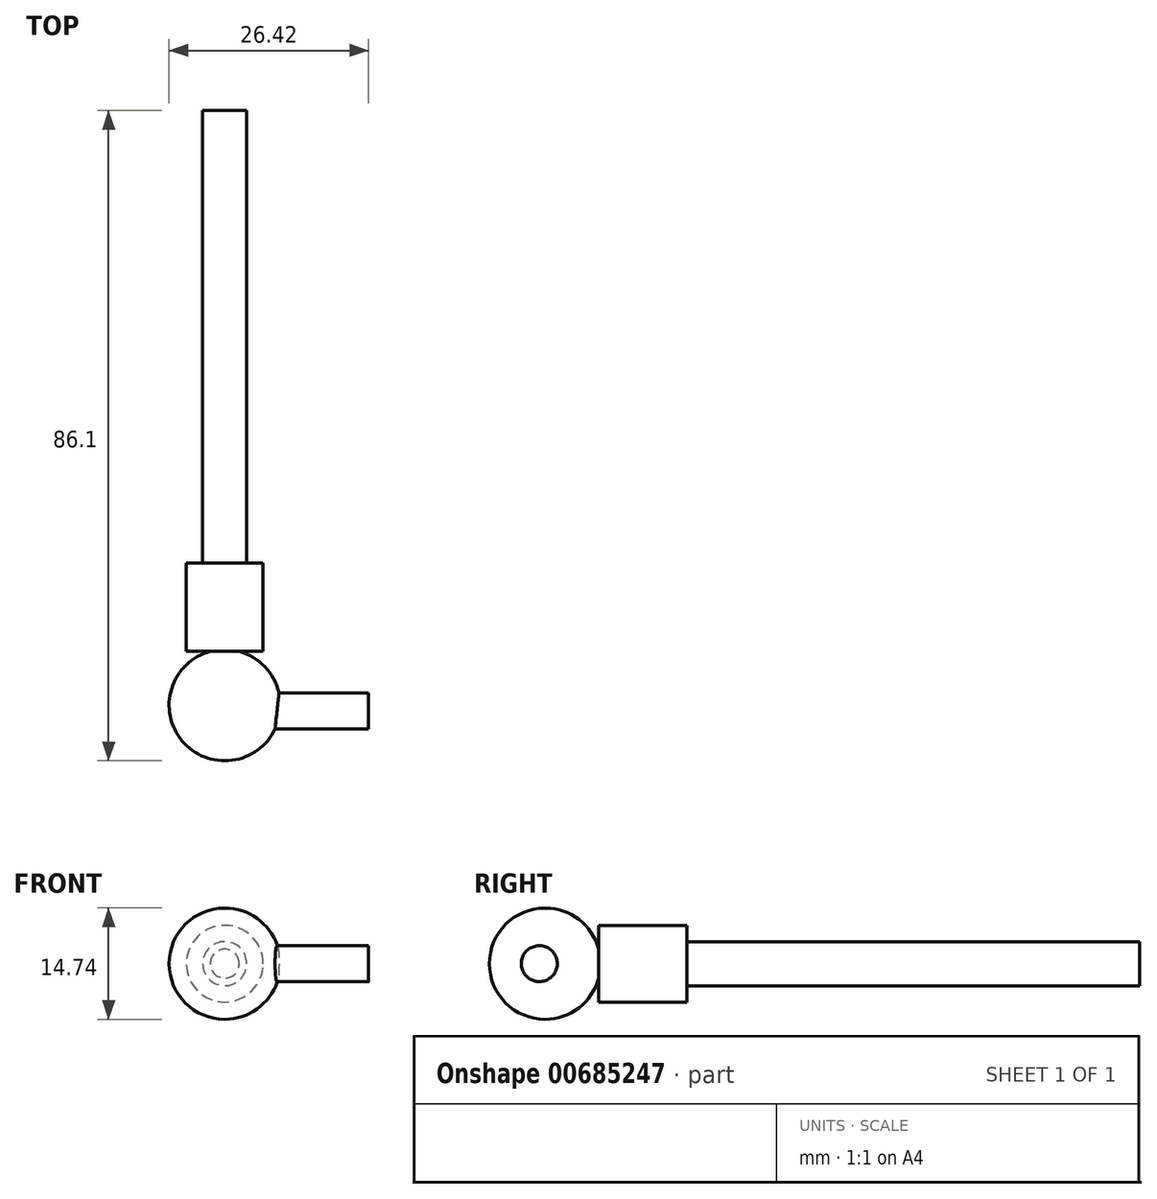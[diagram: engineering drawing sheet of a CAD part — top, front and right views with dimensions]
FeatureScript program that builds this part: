
annotation { "Feature Type Name" : "Feature", "Feature Type Description" : "" }
export const myFeature = defineFeature(function(context is Context, id is Id, definition is map)
    precondition{}
    {
        {
            var Q0;
            Q0=qCreatedBy(makeId("Front.planeOp"),FACE);
            var sketch = newSketch(context, id + "F0", { "sketchPlane" : qUnion([Q0])});
            skCircle(sketch, "E0", {"center": v(0, 0) * mm, "radius": 5.08 * mm});
            skSolve(sketch);
        }
        {
            var Q0;
            Q0 = qSketchRegion(id + "F0", true);
            extrude(context, id + "F1", {"entities" : qUnion([Q0]), "depth" : 11.68 * mm, "offsetDistance" : 25.4 * mm});
        }
        {
            var Q0;
            Q0=qCreatedBy(makeId("Right.planeOp"),FACE);
            var sketch = newSketch(context, id + "F2", { "sketchPlane" : qUnion([Q0])});
            skCircle(sketch, "E1", {"center": v(-18.8, 0) * mm, "radius": 7.37 * mm});
            skLineSegment(sketch, "E2", {"start": v(-18.8, 0) * mm, "end": v(-18.8, 7.37) * mm});
            skLineSegment(sketch, "E3", {"start": v(-18.8, 7.37) * mm, "end": v(-18.8, -7.37) * mm});
            skSolve(sketch);
        }
        {
            var Q0;
            {var subQ0=sQuery(id+"F2.wireOp",EDGE,"E3");var subQ4=makeQuery(id+"F2.imprint","IMPRINT",VERTEX,{"derivedFrom":subQ0});Q0=makeQuery(id+"F2.imprint","IMPRINT",FACE,{"disambiguationData":[TD([[makeQuery(id+"F2.imprint","IMPRINT",EDGE,{"disambiguationData":[TD([[subQ4,1.0]])],"derivedFrom":subQ0}),-1.0]])]});}
            var Q1;
            Q1=sQuery(id+"F2.wireOp",EDGE,"E3");
            revolve(context, id + "F3", {"operationType" : NewBodyOperationType.ADD, "entities" : qUnion([Q0]), "axis" : qUnion([Q1]), "revolveType" : RevolveType.FULL});
        }
        {
            var Q0;
            Q0=makeQuery(id+"F1.opExtrude","CAP_FACE",FACE,{"disambiguationData":[OSD([sQuery(id+"F0.wireOp",EDGE,"E0")])],"isStart":true});
            var sketch = newSketch(context, id + "F4", { "sketchPlane" : qUnion([Q0])});
            skCircle(sketch, "E4", {"center": v(0, 0) * mm, "radius": 2.92 * mm});
            skSolve(sketch);
        }
        {
            var Q0;
            Q0 = qSketchRegion(id + "F4", true);
            extrude(context, id + "F5", {"entities" : qUnion([Q0]), "operationType" : NewBodyOperationType.ADD, "depth" : 59.94 * mm, "offsetDistance" : 25.4 * mm});
        }
        {
            var Q0;
            Q0=qCreatedBy(makeId("Right.planeOp"),FACE);
            var sketch = newSketch(context, id + "F6", { "sketchPlane" : qUnion([Q0])});
            skCircle(sketch, "E5", {"center": v(-19.56, 0) * mm, "radius": 2.38 * mm});
            skSolve(sketch);
        }
        {
            var Q0;
            Q0 = qSketchRegion(id + "F6", true);
            extrude(context, id + "F7", {"entities" : qUnion([Q0]), "operationType" : NewBodyOperationType.ADD, "depth" : 19.05 * mm, "offsetDistance" : 25.4 * mm});
        }
    });
